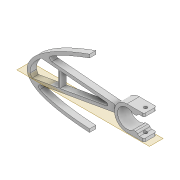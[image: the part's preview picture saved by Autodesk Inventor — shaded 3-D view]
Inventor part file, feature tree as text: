
AUTODESK INVENTOR PART (.ipt)
format: ipt  version: 2022 (Build 260153000, 153)  size: 602,624 bytes
history: native  units: mm
features: extrude x6, sketch x5, fillet x3, projected_geometry x3, shell x1
ambient origin geometry x8: Origin, YZ Plane, XZ Plane, XY Plane, X Axis, Y Axis, Z Axis, Center Point
bodies: Solid1 (feature_tree)
feature tree (18):
  extrude  "Extrusion1"  Depth=2.0mm
  shell  "Shell1"  Thickness=66.0mm
  extrude  "Extrusion9"  Depth=2.0mm
  fillet  "Fillet2"  Radius=2.0mm
  extrude  "Extrusion10"  Depth=11.0mm
  extrude  "Extrusion12"  Depth=1.745329mm
  extrude  "Extrusion15"  Depth=2.0mm
  extrude  "Extrusion16"  Depth=2.0mm
  fillet  "Fillet4"  Radius=1.0mm
  fillet  "Fillet5"  Radius=1.5mm
  sketch  "Sketch3"  dims[d0=4.0mm d1=0.0mm d2=2.0mm d68=66.0mm]
  sketch  "Sketch25"  dims[d69=8.05mm d70=12.0mm d71=2.0mm]
  projected_geometry  "Projected Loop13"
  sketch  "Sketch26"  dims[d72=11.0mm d73=11.0mm]
  sketch  "Sketch28"  dims[d74=0.872665mm d75=1.745329mm]
  projected_geometry  "Projected Loop17"
  sketch  "Sketch33"  dims[d76=2.0mm d77=1.0mm d79=2.0mm d80=1.0mm d81=1.5mm d82=1.5mm d83=4.0mm d84=0.0mm d85=3.0mm d86=3.0mm d87=1.5mm d88=40.0mm d89=40.0mm d90=100.0mm d91=0.0mm d98=2.1mm d99=2.0mm d100=2.1mm d102=30.0mm d103=0.0mm d114=3.0mm d115=1.0mm d116=45.0mm d117=2.0mm d118=0.0mm d119=2.0mm d120=0.0mm d121=1.0mm d127=2.0mm d128=0.872665mm d129=0.5mm d130=0.872665mm]
  projected_geometry  "Projected Loop18"
